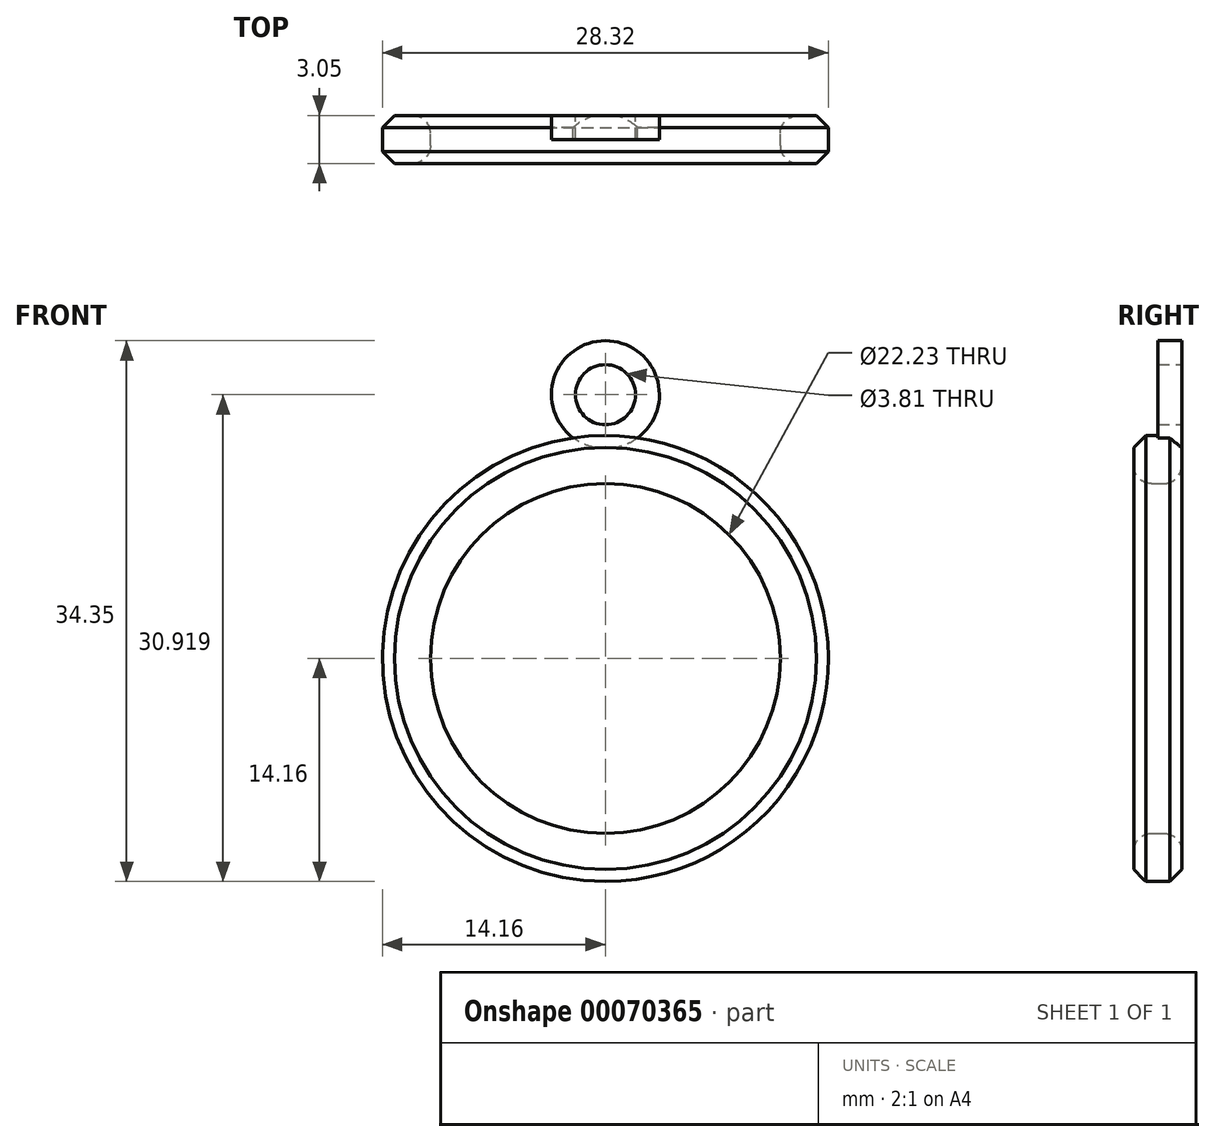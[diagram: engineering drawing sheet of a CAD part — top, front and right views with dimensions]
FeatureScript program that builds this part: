
annotation { "Feature Type Name" : "Feature", "Feature Type Description" : "" }
export const myFeature = defineFeature(function(context is Context, id is Id, definition is map)
    precondition{}
    {
        {
            var Q0;
            Q0=qCreatedBy(makeId("Front.planeOp"),FACE);
            var sketch = newSketch(context, id + "F0", { "sketchPlane" : qUnion([Q0])});
            skCircle(sketch, "E0", {"center": v(0, 0) * mm, "radius": 11.11 * mm});
            skCircle(sketch, "E1", {"center": v(0, 16.76) * mm, "radius": 1.9 * mm});
            skCircle(sketch, "E2.0", {"center": v(0, 0) * mm, "radius": 14.16 * mm});
            skCircle(sketch, "E3.0", {"center": v(0, 16.76) * mm, "radius": 3.43 * mm});
            skSolve(sketch);
        }
        {
            var Q0;
            Q0=makeQuery(id+"F0.imprint","IMPRINT",FACE,{"disambiguationData":[TD([[makeQuery(id+"F0.imprint","IMPRINT",EDGE,{"derivedFrom":sQuery(id+"F0.wireOp",EDGE,"E0")}),-1.0]])]});
            var Q1;
            {var subQ0=sQuery(id+"F0.wireOp",EDGE,"E3.0");var subQ1=sQuery(id+"F0.wireOp",EDGE,"E2.0");var subQ2=makeQuery(id+"F0.imprint","INTERSECT",VERTEX,{"disambiguationData":[OD(0.0)],"derivedFrom":[subQ1,subQ0]});Q1=makeQuery(id+"F0.imprint","IMPRINT",FACE,{"disambiguationData":[TD([[makeQuery(id+"F0.imprint","IMPRINT",EDGE,{"disambiguationData":[TD([[subQ2,1.0]])],"derivedFrom":subQ1}),1.0]])]});}
            extrude(context, id + "F1", {"entities" : qUnion([Q0, Q1]), "depth" : 3.05 * mm});
        }
        {
            var Q0;
            Q0=makeQuery(id+"F0.imprint","IMPRINT",FACE,{"disambiguationData":[TD([[makeQuery(id+"F0.imprint","IMPRINT",EDGE,{"derivedFrom":sQuery(id+"F0.wireOp",EDGE,"E1")}),-1.0]])]});
            extrude(context, id + "F2", {"entities" : qUnion([Q0]), "operationType" : NewBodyOperationType.ADD, "depth" : 1.52 * mm});
        }
        {
            var Q0;
            Q0=makeQuery(id+"F1.opExtrude","SWEPT_FACE",FACE,{"disambiguationData":[OSD([sQuery(id+"F0.wireOp",EDGE,"E0")])]});
            fillet(context, id + "F3", {"entities" : qUnion([Q0]), "radius" : 1.13 * mm, "tangentPropagation" : true, "allowEdgeOverflow" : false});
        }
        {
            var Q0;
            Q0=makeQuery(id+"F1.opExtrude","CAP_EDGE",EDGE,{"disambiguationData":[OSD([sQuery(id+"F0.wireOp",EDGE,"E2.0")])],"isStart":false});
            var Q1;
            Q1=makeQuery(id+"F1.opExtrude","CAP_EDGE",EDGE,{"disambiguationData":[OSD([sQuery(id+"F0.wireOp",EDGE,"E2.0")])],"isStart":true});
            chamfer(context, id + "F4", {"entities" : qUnion([Q0, Q1]), "width" : 0.76 * mm, "tangentPropagation" : true});
        }
    });
